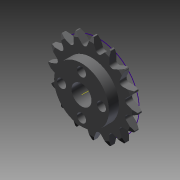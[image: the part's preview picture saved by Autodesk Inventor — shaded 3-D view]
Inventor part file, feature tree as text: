
AUTODESK INVENTOR PART (.ipt)
format: ipt  version: 2015 (Build 190159000, 159)  size: 423,936 bytes
history: native  units: in
note: dims shown in document units (in); Inventor stores cm internally (conversion verified against a paired STEP export)
features: other x14, sketch x1, imported_body x1
ambient origin geometry x8: Origin, YZ Plane, XZ Plane, XY Plane, X Axis, Y Axis, Z Axis, Center Point
bodies: Body1 (feature_tree)
feature tree (16):
  other  "tetrix_739165_2012"
  other  "tetrix_739165_20121"
  other  "A_1"
  other  "A_2"
  other  "A_4"
  other  "A_5"
  other  "A_6"
  other  "A_3"
  other  "A_7"
  other  "A_8"
  other  "A_9"
  other  "FRONT"
  other  "TOP"
  other  "RIGHT"
  sketch  "Sketch1"
  imported_body  "Base1"
